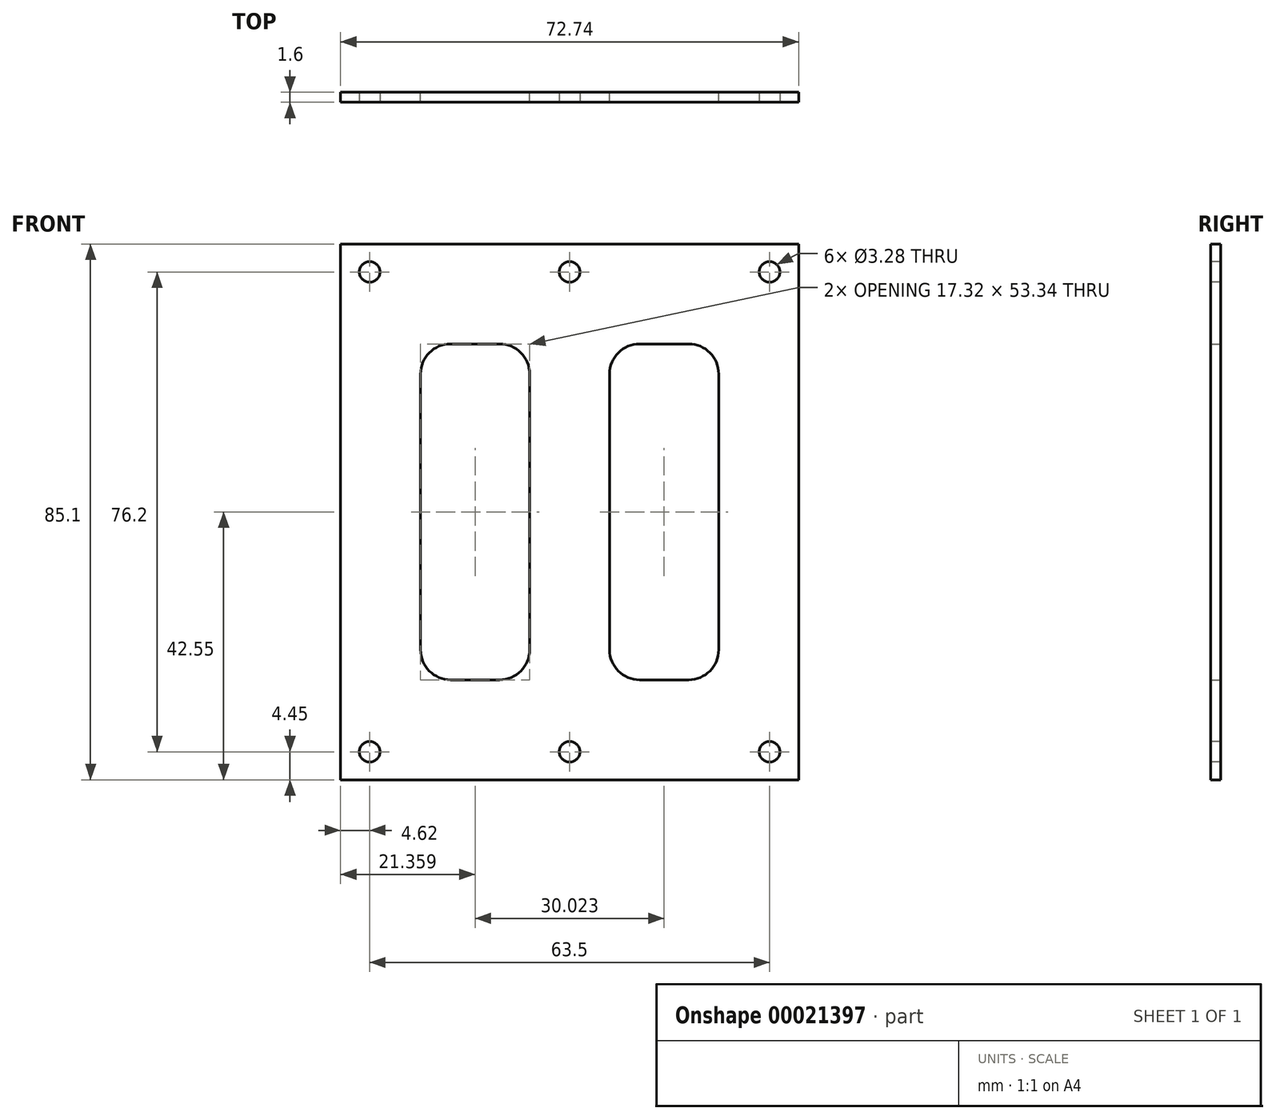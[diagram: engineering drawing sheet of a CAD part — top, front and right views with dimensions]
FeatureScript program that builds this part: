
annotation { "Feature Type Name" : "Feature", "Feature Type Description" : "" }
export const myFeature = defineFeature(function(context is Context, id is Id, definition is map)
    precondition{}
    {
        {
            var Q0;
            Q0=qCreatedBy(makeId("Front.planeOp"),FACE);
            var sketch = newSketch(context, id + "F0", { "sketchPlane" : qUnion([Q0])});
            skLineSegment(sketch, "E0.rect.bottom", {"start": v(36.37, -42.55) * mm, "end": v(-36.37, -42.55) * mm});
            skLineSegment(sketch, "E0.rect.top", {"start": v(36.37, 42.55) * mm, "end": v(-36.37, 42.55) * mm});
            skLineSegment(sketch, "E0.rect.left", {"start": v(36.37, -42.55) * mm, "end": v(36.37, 42.55) * mm});
            skLineSegment(sketch, "E0.rect.right", {"start": v(-36.37, -42.55) * mm, "end": v(-36.37, 42.55) * mm});
            skPoint(sketch, "E0.rect.middle", {"position": v(0, 0) * mm});
            skLineSegment(sketch, "E1.rect.bottom", {"start": v(-23.67, -26.67) * mm, "end": v(-6.35, -26.67) * mm});
            skLineSegment(sketch, "E1.rect.top", {"start": v(-23.67, 26.67) * mm, "end": v(-6.35, 26.67) * mm});
            skLineSegment(sketch, "E1.rect.left", {"start": v(-23.67, -26.67) * mm, "end": v(-23.67, 26.67) * mm});
            skLineSegment(sketch, "E1.rect.right", {"start": v(-6.35, -26.67) * mm, "end": v(-6.35, 26.67) * mm});
            skPoint(sketch, "E1.rect.middle", {"position": v(-15.01, 0) * mm});
            skLineSegment(sketch, "E2.rect.bottom", {"start": v(6.35, -26.67) * mm, "end": v(23.67, -26.67) * mm});
            skLineSegment(sketch, "E2.rect.top", {"start": v(6.35, 26.67) * mm, "end": v(23.67, 26.67) * mm});
            skLineSegment(sketch, "E2.rect.left", {"start": v(6.35, -26.67) * mm, "end": v(6.35, 26.67) * mm});
            skLineSegment(sketch, "E2.rect.right", {"start": v(23.67, -26.67) * mm, "end": v(23.67, 26.67) * mm});
            skPoint(sketch, "E2.rect.middle", {"position": v(15.01, 0) * mm});
            skSolve(sketch);
        }
        {
            var Q0;
            Q0=makeQuery(id+"F0.imprint","IMPRINT",FACE,{"disambiguationData":[TD([[makeQuery(id+"F0.imprint","IMPRINT",EDGE,{"derivedFrom":sQuery(id+"F0.wireOp",EDGE,"E0.rect.bottom")}),-1.0]])]});
            extrude(context, id + "F1", {"entities" : qUnion([Q0]), "depth" : 1.6 * mm});
        }
        {
            var Q0;
            Q0=makeQuery(id+"F1.opExtrude","SWEPT_EDGE",EDGE,{"disambiguationData":[OSD([sQuery(id+"F0.wireOp",EDGE,"E1.rect.top"),sQuery(id+"F0.wireOp",EDGE,"E1.rect.left")])]});
            var Q1;
            Q1=makeQuery(id+"F1.opExtrude","SWEPT_EDGE",EDGE,{"disambiguationData":[OSD([sQuery(id+"F0.wireOp",EDGE,"E2.rect.top"),sQuery(id+"F0.wireOp",EDGE,"E2.rect.left")])]});
            var Q2;
            Q2=makeQuery(id+"F1.opExtrude","SWEPT_EDGE",EDGE,{"disambiguationData":[OSD([sQuery(id+"F0.wireOp",EDGE,"E2.rect.top"),sQuery(id+"F0.wireOp",EDGE,"E2.rect.right")])]});
            var Q3;
            Q3=makeQuery(id+"F1.opExtrude","SWEPT_EDGE",EDGE,{"disambiguationData":[OSD([sQuery(id+"F0.wireOp",EDGE,"E1.rect.top"),sQuery(id+"F0.wireOp",EDGE,"E1.rect.right")])]});
            var Q4;
            Q4=makeQuery(id+"F1.opExtrude","SWEPT_EDGE",EDGE,{"disambiguationData":[OSD([sQuery(id+"F0.wireOp",EDGE,"E1.rect.bottom"),sQuery(id+"F0.wireOp",EDGE,"E1.rect.left")])]});
            var Q5;
            Q5=makeQuery(id+"F1.opExtrude","SWEPT_EDGE",EDGE,{"disambiguationData":[OSD([sQuery(id+"F0.wireOp",EDGE,"E2.rect.bottom"),sQuery(id+"F0.wireOp",EDGE,"E2.rect.left")])]});
            var Q6;
            Q6=makeQuery(id+"F1.opExtrude","SWEPT_EDGE",EDGE,{"disambiguationData":[OSD([sQuery(id+"F0.wireOp",EDGE,"E2.rect.bottom"),sQuery(id+"F0.wireOp",EDGE,"E2.rect.right")])]});
            var Q7;
            Q7=makeQuery(id+"F1.opExtrude","SWEPT_EDGE",EDGE,{"disambiguationData":[OSD([sQuery(id+"F0.wireOp",EDGE,"E1.rect.bottom"),sQuery(id+"F0.wireOp",EDGE,"E1.rect.right")])]});
            fillet(context, id + "F2", {"entities" : qUnion([Q0, Q1, Q2, Q3, Q4, Q5, Q6, Q7]), "radius" : 4.78 * mm, "tangentPropagation" : true, "allowEdgeOverflow" : false});
        }
        {
            var Q0;
            Q0=makeQuery(id+"F1.opExtrude","CAP_FACE",FACE,{"disambiguationData":[OSD([sQuery(id+"F0.wireOp",EDGE,"E0.rect.bottom"),sQuery(id+"F0.wireOp",EDGE,"E0.rect.top"),sQuery(id+"F0.wireOp",EDGE,"E0.rect.left"),sQuery(id+"F0.wireOp",EDGE,"E0.rect.right"),sQuery(id+"F0.wireOp",EDGE,"E1.rect.bottom"),sQuery(id+"F0.wireOp",EDGE,"E1.rect.top"),sQuery(id+"F0.wireOp",EDGE,"E1.rect.left"),sQuery(id+"F0.wireOp",EDGE,"E1.rect.right"),sQuery(id+"F0.wireOp",EDGE,"E2.rect.bottom"),sQuery(id+"F0.wireOp",EDGE,"E2.rect.top"),sQuery(id+"F0.wireOp",EDGE,"E2.rect.left"),sQuery(id+"F0.wireOp",EDGE,"E2.rect.right")])],"isStart":false});
            var sketch = newSketch(context, id + "F3", { "sketchPlane" : qUnion([Q0])});
            skLineSegment(sketch, "E3.rect.bottom", {"start": v(31.75, -38.1) * mm, "end": v(-31.75, -38.1) * mm});
            skLineSegment(sketch, "E3.rect.top", {"start": v(31.75, 38.1) * mm, "end": v(-31.75, 38.1) * mm});
            skLineSegment(sketch, "E3.rect.left", {"start": v(31.75, -38.1) * mm, "end": v(31.75, 38.1) * mm});
            skLineSegment(sketch, "E3.rect.right", {"start": v(-31.75, -38.1) * mm, "end": v(-31.75, 38.1) * mm});
            skPoint(sketch, "E3.rect.middle", {"position": v(0, 0) * mm});
            skLineSegment(sketch, "E4", {"start": v(0, 38.1) * mm, "end": v(0, -38.1) * mm});
            skSolve(sketch);
        }
        {
            var Q0;
            Q0=sQuery(id+"F3.wireOp",VERTEX,"E3.rect.right.end");
            var Q1;
            Q1=sQuery(id+"F3.wireOp",VERTEX,"E4.start");
            var Q2;
            Q2=sQuery(id+"F3.wireOp",VERTEX,"E3.rect.left.end");
            var Q3;
            Q3=sQuery(id+"F3.wireOp",VERTEX,"E3.rect.bottom.start");
            var Q4;
            Q4=sQuery(id+"F3.wireOp",VERTEX,"E4.end");
            var Q5;
            Q5=sQuery(id+"F3.wireOp",VERTEX,"E3.rect.right.start");
            var Q6;
            Q6=makeQuery(id+"F1.opExtrude","SWEPT_BODY",BODY,{"disambiguationData":[OSD([sQuery(id+"F0.wireOp",EDGE,"E0.rect.bottom"),sQuery(id+"F0.wireOp",EDGE,"E0.rect.top"),sQuery(id+"F0.wireOp",EDGE,"E0.rect.left"),sQuery(id+"F0.wireOp",EDGE,"E0.rect.right"),sQuery(id+"F0.wireOp",EDGE,"E1.rect.bottom"),sQuery(id+"F0.wireOp",EDGE,"E1.rect.top"),sQuery(id+"F0.wireOp",EDGE,"E1.rect.left"),sQuery(id+"F0.wireOp",EDGE,"E1.rect.right"),sQuery(id+"F0.wireOp",EDGE,"E2.rect.bottom"),sQuery(id+"F0.wireOp",EDGE,"E2.rect.top"),sQuery(id+"F0.wireOp",EDGE,"E2.rect.left"),sQuery(id+"F0.wireOp",EDGE,"E2.rect.right")])]});
            hole(context, id + "F4", {"style" : HoleStyle.SIMPLE, "holeDiameter" : 3.28 * mm, "endStyle" : HoleEndStyle.THROUGH, "locations" : qUnion([Q0, Q1, Q2, Q3, Q4, Q5]), "scope" : qUnion([Q6])});
        }
    });
